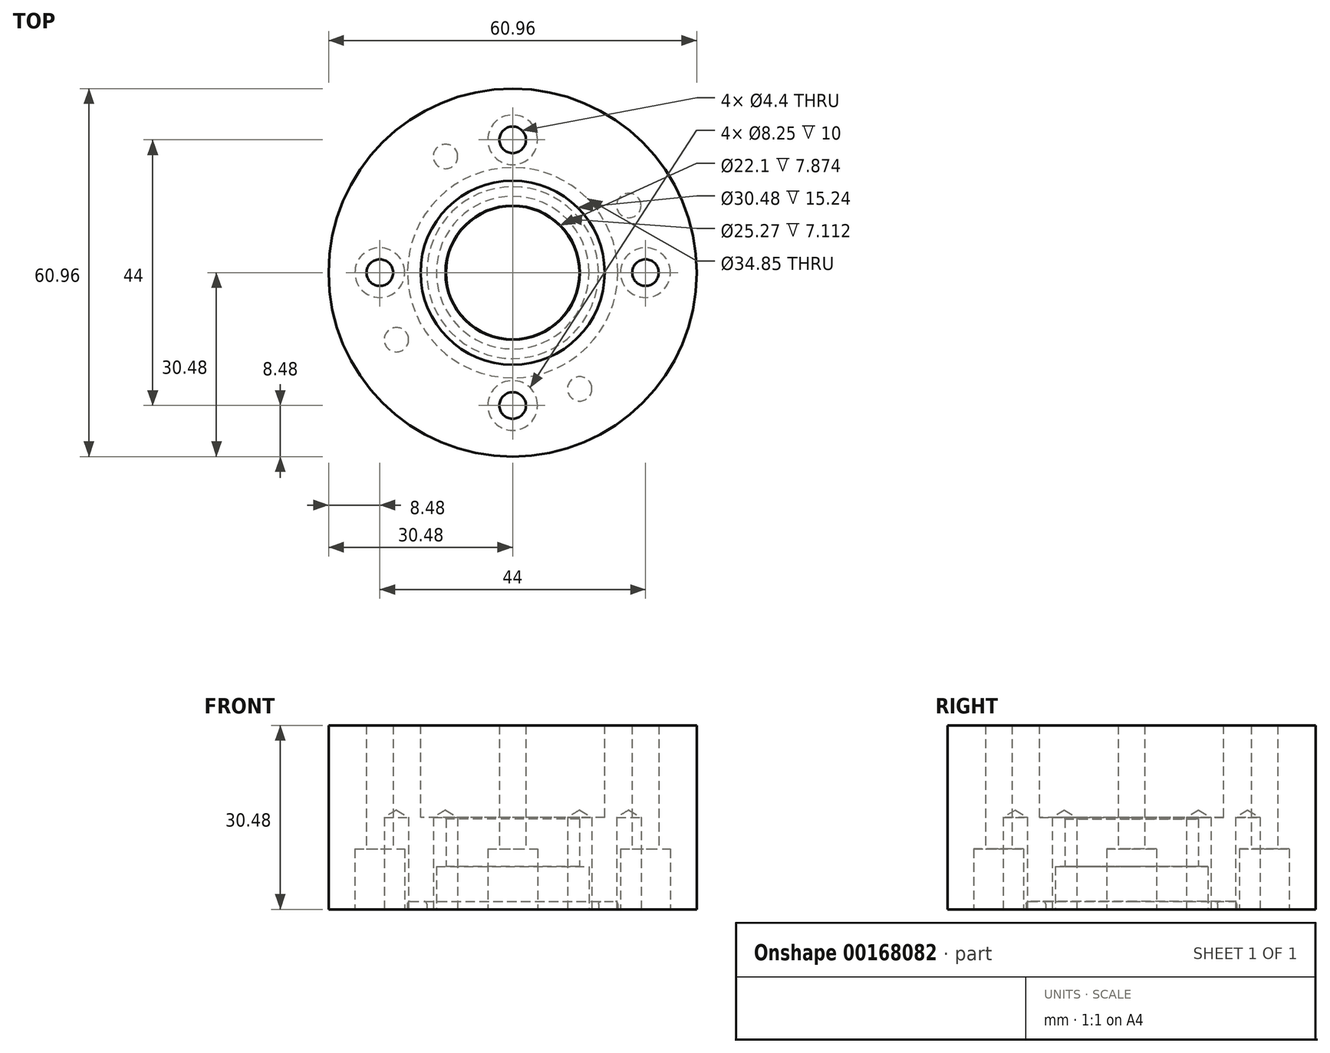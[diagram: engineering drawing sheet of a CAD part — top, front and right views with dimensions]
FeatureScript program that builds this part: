
annotation { "Feature Type Name" : "Feature", "Feature Type Description" : "" }
export const myFeature = defineFeature(function(context is Context, id is Id, definition is map)
    precondition{}
    {
        {
            var Q0;
            Q0=qCreatedBy(makeId("Top.planeOp"),FACE);
            var sketch = newSketch(context, id + "F0", { "sketchPlane" : qUnion([Q0])});
            skCircle(sketch, "E0", {"center": v(0, 0) * mm, "radius": 30.48 * mm});
            skCircle(sketch, "E1", {"center": v(0, 0) * mm, "radius": 11.05 * mm});
            skSolve(sketch);
        }
        {
            var Q0;
            Q0=qSketchRegion(id+"F0",true);
            extrude(context, id + "F1", {"entities" : qUnion([Q0]), "depth" : 30.48 * mm});
        }
        {
            var Q0;
            Q0=makeQuery(id+"F1.opExtrude","CAP_FACE",FACE,{"disambiguationData":[OSD([sQuery(id+"F0.wireOp",EDGE,"E0"),sQuery(id+"F0.wireOp",EDGE,"E1")])],"isStart":false});
            var sketch = newSketch(context, id + "F2", { "sketchPlane" : qUnion([Q0])});
            skCircle(sketch, "E2", {"center": v(0, 0) * mm, "radius": 15.24 * mm});
            skSolve(sketch);
        }
        {
            var Q0;
            Q0 = qSketchRegion(id + "F2", true);
            extrude(context, id + "F3", {"entities" : qUnion([Q0]), "operationType" : NewBodyOperationType.REMOVE, "oppositeDirection" : true, "depth" : 15.24 * mm});
        }
        {
            var Q0;
            Q0=makeQuery(id+"F1.opExtrude","CAP_FACE",FACE,{"disambiguationData":[OSD([sQuery(id+"F0.wireOp",EDGE,"E0"),sQuery(id+"F0.wireOp",EDGE,"E1")])],"isStart":true});
            var sketch = newSketch(context, id + "F4", { "sketchPlane" : qUnion([Q0])});
            skCircle(sketch, "E3", {"center": v(0, 0) * mm, "radius": 12.64 * mm});
            skCircle(sketch, "E4.0", {"center": v(0, 0) * mm, "radius": 11.05 * mm});
            skSolve(sketch);
        }
        {
            var Q0;
            Q0 = qSketchRegion(id + "F4", true);
            extrude(context, id + "F5", {"entities" : qUnion([Q0]), "operationType" : NewBodyOperationType.REMOVE, "oppositeDirection" : true, "depth" : 7.11 * mm});
        }
        {
            var Q0;
            Q0=makeQuery(id+"F3.boolean.opBoolean","INTERSECT",EDGE,{"derivedFrom":[makeQuery(id+"F1.opExtrude","SWEPT_FACE",FACE,{"disambiguationData":[OSD([sQuery(id+"F0.wireOp",EDGE,"E1")])]}),makeQuery(id+"F3.opExtrude","CAP_FACE",FACE,{"disambiguationData":[OSD([sQuery(id+"F2.wireOp",EDGE,"E2")])],"isStart":false})]});
            var Q1;
            Q1=makeQuery(id+"F5.boolean.opBoolean","COPY",EDGE,{"derivedFrom":makeQuery(id+"F5.opExtrude","CAP_EDGE",EDGE,{"disambiguationData":[OSD([sQuery(id+"F4.wireOp",EDGE,"E3")])],"isStart":true})});
            var Q2;
            Q2=makeQuery(id+"F5.boolean.opBoolean","COPY",EDGE,{"derivedFrom":makeQuery(id+"F5.opExtrude","CAP_EDGE",EDGE,{"disambiguationData":[OSD([sQuery(id+"F4.wireOp",EDGE,"E4.0")])],"isStart":false})});
            chamfer(context, id + "F6", {"entities" : qUnion([Q0, Q1, Q2]), "chamferType" : ChamferType.OFFSET_ANGLE, "width" : 0.25 * mm, "oppositeDirection" : false, "angle" : 15 * degree, "tangentPropagation" : true});
        }
        {
            var Q0;
            Q0=makeQuery(id+"F1.opExtrude","CAP_FACE",FACE,{"disambiguationData":[OSD([sQuery(id+"F0.wireOp",EDGE,"E0"),sQuery(id+"F0.wireOp",EDGE,"E1")])],"isStart":true});
            var sketch = newSketch(context, id + "F7", { "sketchPlane" : qUnion([Q0])});
            skPoint(sketch, "E5", {"position": v(0, -22) * mm});
            skPoint(sketch, "E6.1.0", {"position": v(22, 0) * mm});
            skPoint(sketch, "E6.2.0", {"position": v(0, 22) * mm});
            skPoint(sketch, "E6.3.0", {"position": v(-22, 0) * mm});
            skPoint(sketch, "E6.center", {"position": v(0, 0) * mm});
            skSolve(sketch);
        }
        {
            var Q0;
            Q0=sQuery(id+"F7.wireOp",VERTEX,"E5");
            var Q1;
            Q1=sQuery(id+"F7.wireOp",VERTEX,"E6.3.0");
            var Q2;
            Q2=sQuery(id+"F7.wireOp",VERTEX,"E6.2.0");
            var Q3;
            Q3=sQuery(id+"F7.wireOp",VERTEX,"E6.1.0");
            var Q4;
            Q4=makeQuery(id+"F1.opExtrude","SWEPT_BODY",BODY,{"disambiguationData":[OSD([sQuery(id+"F0.wireOp",EDGE,"E0"),sQuery(id+"F0.wireOp",EDGE,"E1")])]});
            hole(context, id + "F8", {"style" : HoleStyle.C_BORE, "endStyle" : HoleEndStyle.THROUGH, "holeDiameter" : 4.4 * mm, "cBoreDiameter" : 8.25 * mm, "cBoreDepth" : 10 * mm, "locations" : qUnion([Q0, Q1, Q2, Q3]), "scope" : qUnion([Q4]), "isTappedThrough" : true});
        }
        {
            var Q0;
            Q0=makeQuery(id+"F1.opExtrude","CAP_FACE",FACE,{"disambiguationData":[OSD([sQuery(id+"F0.wireOp",EDGE,"E0"),sQuery(id+"F0.wireOp",EDGE,"E1")])],"isStart":true});
            var sketch = newSketch(context, id + "F9", { "sketchPlane" : qUnion([Q0])});
            skLineSegment(sketch, "E7", {"start": v(0, 0) * mm, "end": v(-19.25, 11.11) * mm, "construction": true});
            skPoint(sketch, "E8", {"position": v(-19.25, 11.11) * mm});
            skPoint(sketch, "E9.1.0", {"position": v(-11.11, -19.25) * mm});
            skPoint(sketch, "E9.2.0", {"position": v(19.25, -11.11) * mm});
            skPoint(sketch, "E9.3.0", {"position": v(11.11, 19.25) * mm});
            skPoint(sketch, "E9.center", {"position": v(0, 0) * mm});
            skSolve(sketch);
        }
        {
            var Q0;
            Q0=sQuery(id+"F9.wireOp",VERTEX,"E8");
            var Q1;
            Q1=sQuery(id+"F9.wireOp",VERTEX,"E9.3.0");
            var Q2;
            Q2=sQuery(id+"F9.wireOp",VERTEX,"E9.2.0");
            var Q3;
            Q3=sQuery(id+"F9.wireOp",VERTEX,"E9.1.0");
            var Q4;
            Q4=makeQuery(id+"F1.opExtrude","SWEPT_BODY",BODY,{"disambiguationData":[OSD([sQuery(id+"F0.wireOp",EDGE,"E0"),sQuery(id+"F0.wireOp",EDGE,"E1")])]});
            hole(context, id + "F10", {"style" : HoleStyle.SIMPLE, "endStyle" : HoleEndStyle.BLIND, "standardTappedOrClearance" : lookupTablePath({ "standard" : "ANSI", "engagement" : "75%", "pitch" : "32 tpi", "size" : "#10", "type" : "Tapped" }), "standardBlindInLast" : lookupTablePath({ "standard" : "ANSI", "engagement" : "75%", "pitch" : "32 tpi", "size" : "#10", "type" : "Tapped" }), "holeDiameter" : 4.04 * mm, "holeDepth" : 15.24 * mm, "locations" : qUnion([Q0, Q1, Q2, Q3]), "scope" : qUnion([Q4]), "majorDiameter" : 4.83 * mm});
        }
        {
            var Q0;
            Q0=makeQuery(id+"F1.opExtrude","CAP_FACE",FACE,{"disambiguationData":[OSD([sQuery(id+"F0.wireOp",EDGE,"E0"),sQuery(id+"F0.wireOp",EDGE,"E1")])],"isStart":true});
            var sketch = newSketch(context, id + "F11", { "sketchPlane" : qUnion([Q0])});
            skCircle(sketch, "E10", {"center": v(0, 0) * mm, "radius": 14.22 * mm});
            skCircle(sketch, "E11", {"center": v(0, 0) * mm, "radius": 17.42 * mm});
            skCircle(sketch, "E12", {"center": v(0, 0) * mm, "radius": 15.82 * mm, "construction": true});
            skSolve(sketch);
        }
        {
            var Q0;
            Q0 = qSketchRegion(id + "F11", true);
            extrude(context, id + "F12", {"entities" : qUnion([Q0]), "operationType" : NewBodyOperationType.REMOVE, "oppositeDirection" : true, "depth" : 1.3 * mm});
        }
        {
            var Q0;
            Q0=makeQuery(id+"F12.boolean.opBoolean","COPY",EDGE,{"derivedFrom":makeQuery(id+"F12.opExtrude","CAP_EDGE",EDGE,{"disambiguationData":[OSD([sQuery(id+"F11.wireOp",EDGE,"E10")])],"isStart":false})});
            var Q1;
            Q1=makeQuery(id+"F12.boolean.opBoolean","COPY",EDGE,{"derivedFrom":makeQuery(id+"F12.opExtrude","CAP_EDGE",EDGE,{"disambiguationData":[OSD([sQuery(id+"F11.wireOp",EDGE,"E11")])],"isStart":false})});
            fillet(context, id + "F13", {"entities" : qUnion([Q0, Q1]), "radius" : 0.4 * mm, "tangentPropagation" : true, "allowEdgeOverflow" : false});
        }
    });
